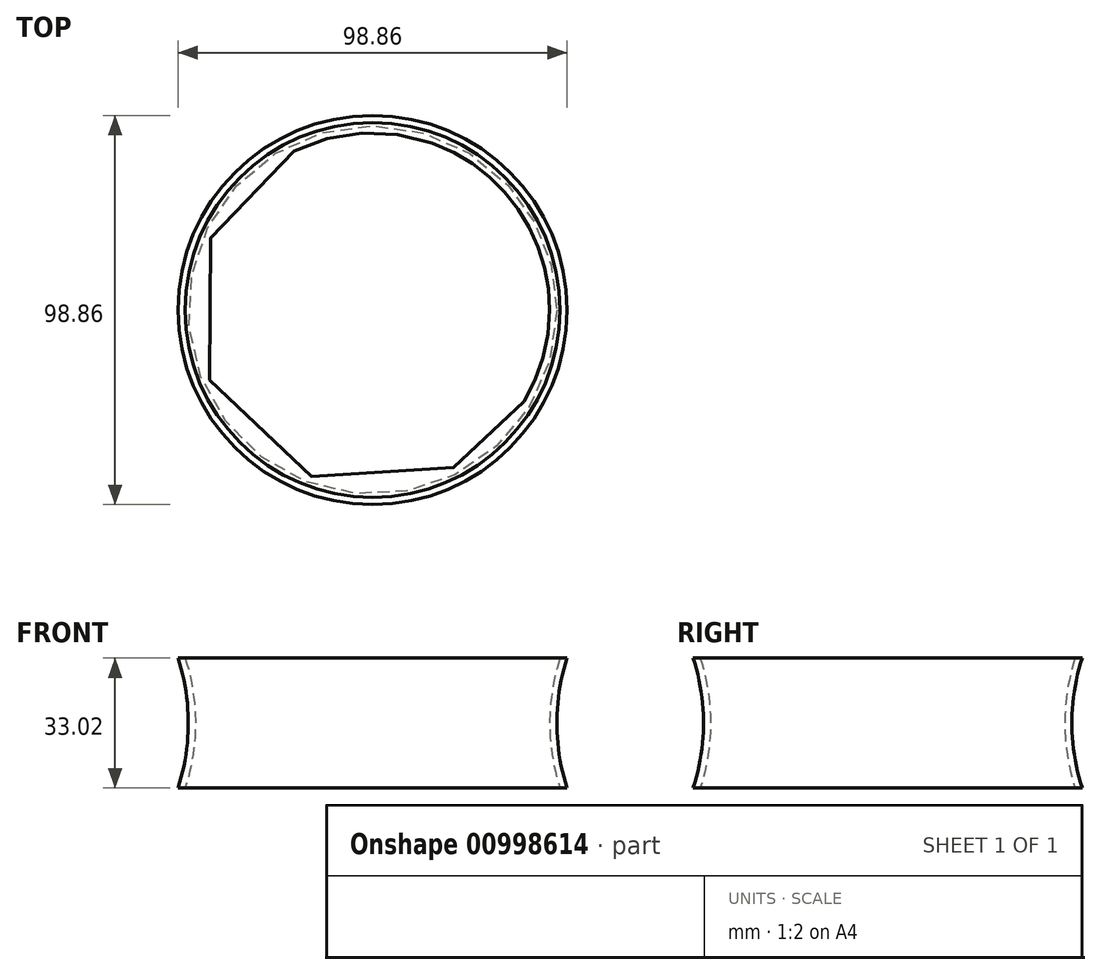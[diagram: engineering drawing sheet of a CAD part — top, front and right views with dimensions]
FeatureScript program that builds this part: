
annotation { "Feature Type Name" : "Feature", "Feature Type Description" : "" }
export const myFeature = defineFeature(function(context is Context, id is Id, definition is map)
    precondition{}
    {
        {
            var Q0;
            Q0=qCreatedBy(makeId("Front.planeOp"),FACE);
            var sketch = newSketch(context, id + "F0", { "sketchPlane" : qUnion([Q0])});
            skLineSegment(sketch, "E0", {"start": v(0, 61.21) * mm, "end": v(0, -86.97) * mm, "construction": true});
            skPoint(sketch, "E1", {"position": v(-47.63, 0) * mm});
            skPoint(sketch, "E2", {"position": v(-98.43, 0) * mm});
            skPoint(sketch, "E3", {"position": v(-47.62, 16.51) * mm});
            skPoint(sketch, "E4", {"position": v(-47.62, -16.51) * mm});
            skArc(sketch, "E5", {"start": v(-47.62, 16.51) * mm, "mid": v(-45, 0) * mm, "end": v(-47.63, -16.51) * mm});
            skPoint(sketch, "E6", {"position": v(-100.23, 0) * mm});
            skPoint(sketch, "E7", {"position": v(-49.42, 16.51) * mm});
            skPoint(sketch, "E8", {"position": v(-49.42, -16.51) * mm});
            skArc(sketch, "E9", {"start": v(-49.42, 16.51) * mm, "mid": v(-46.8, 0) * mm, "end": v(-49.43, -16.51) * mm});
            skLineSegment(sketch, "E10", {"start": v(-49.42, 16.51) * mm, "end": v(-47.62, 16.51) * mm});
            skLineSegment(sketch, "E11", {"start": v(-49.42, -16.51) * mm, "end": v(-47.62, -16.51) * mm});
            skSolve(sketch);
        }
        {
            var Q0;
            Q0 = qSketchRegion(id + "F0", true);
            var Q1;
            Q1=sQuery(id+"F0.wireOp",EDGE,"E0");
            revolve(context, id + "F1", {"surfaceOperationType" : NewSurfaceOperationType.NEW, "entities" : qUnion([Q0]), "axis" : qUnion([Q1]), "revolveType" : RevolveType.FULL});
        }
    });
